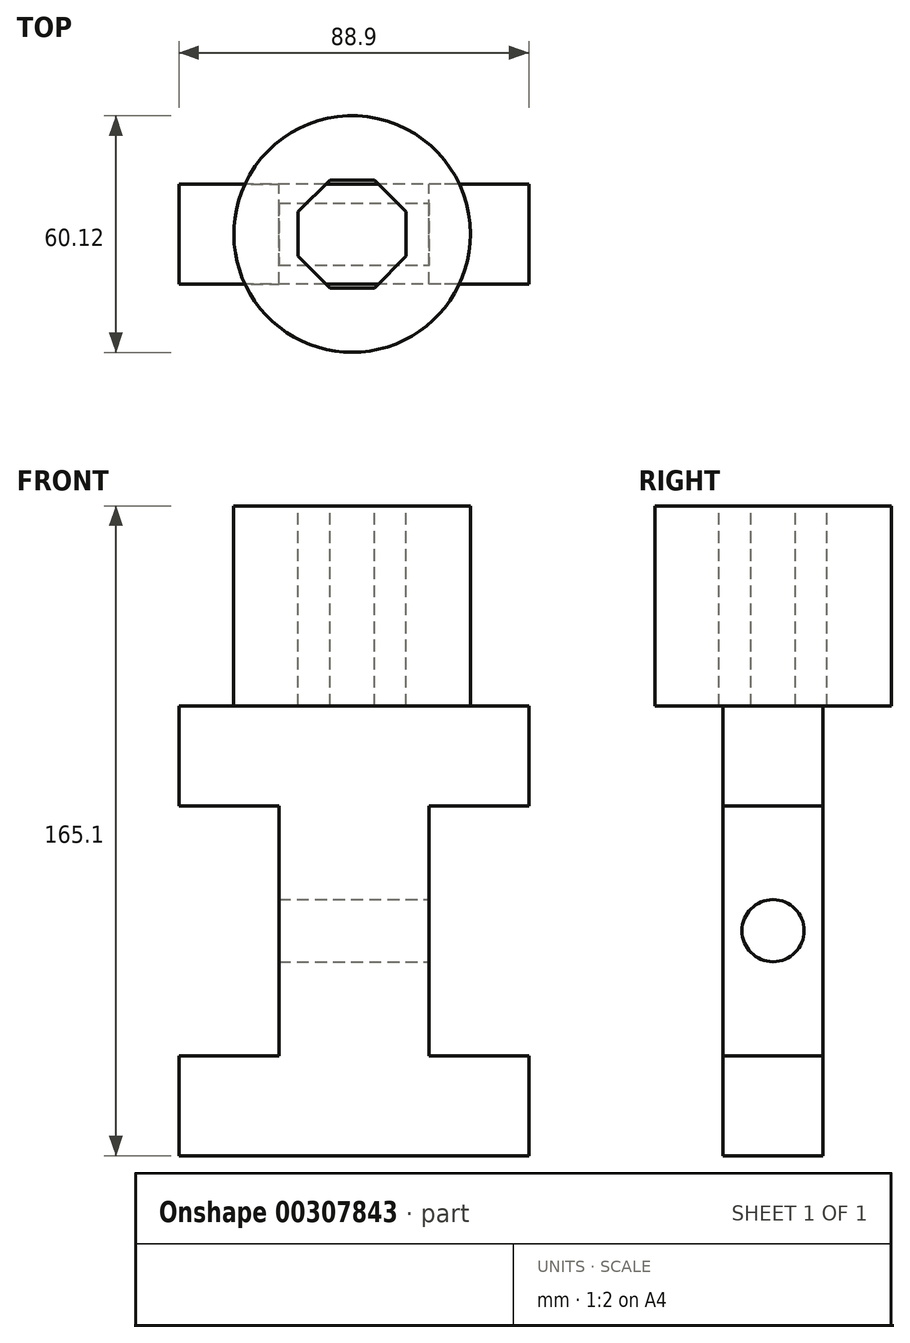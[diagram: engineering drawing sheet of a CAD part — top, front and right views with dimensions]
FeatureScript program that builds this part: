
annotation { "Feature Type Name" : "Feature", "Feature Type Description" : "" }
export const myFeature = defineFeature(function(context is Context, id is Id, definition is map)
    precondition{}
    {
        {
            var Q0;
            Q0=qCreatedBy(makeId("Front.planeOp"),FACE);
            var sketch = newSketch(context, id + "F0", { "sketchPlane" : qUnion([Q0])});
            skLineSegment(sketch, "E0", {"start": v(-44.02, -48.86) * mm, "end": v(44.88, -48.86) * mm});
            skLineSegment(sketch, "E1", {"start": v(44.88, -48.86) * mm, "end": v(44.88, -23.46) * mm});
            skLineSegment(sketch, "E2", {"start": v(44.88, -23.46) * mm, "end": v(19.48, -23.46) * mm});
            skLineSegment(sketch, "E3", {"start": v(19.48, -23.46) * mm, "end": v(19.48, 40.04) * mm});
            skLineSegment(sketch, "E4", {"start": v(19.48, 40.04) * mm, "end": v(44.88, 40.04) * mm});
            skLineSegment(sketch, "E5", {"start": v(44.88, 40.04) * mm, "end": v(44.88, 65.44) * mm});
            skLineSegment(sketch, "E6", {"start": v(44.88, 65.44) * mm, "end": v(-44.02, 65.44) * mm});
            skLineSegment(sketch, "E7", {"start": v(-44.02, 65.44) * mm, "end": v(-44.02, 40.04) * mm});
            skLineSegment(sketch, "E8", {"start": v(-44.02, 40.04) * mm, "end": v(-18.62, 40.04) * mm});
            skLineSegment(sketch, "E9", {"start": v(-18.62, 40.04) * mm, "end": v(-18.62, -23.46) * mm});
            skLineSegment(sketch, "E10", {"start": v(-18.62, -23.46) * mm, "end": v(-44.02, -23.46) * mm});
            skLineSegment(sketch, "E11", {"start": v(-44.02, -23.46) * mm, "end": v(-44.02, -48.86) * mm});
            skSolve(sketch);
        }
        {
            var Q0;
            Q0=makeQuery(id+"F0.imprint","IMPRINT",FACE,{"disambiguationData":[TD([[makeQuery(id+"F0.imprint","IMPRINT",EDGE,{"derivedFrom":sQuery(id+"F0.wireOp",EDGE,"E0")}),1.0]])]});
            extrude(context, id + "F1", {"entities" : qUnion([Q0]), "depth" : 25.4 * mm});
        }
        {
            var Q0;
            Q0=makeQuery(id+"F1.opExtrude","SWEPT_FACE",FACE,{"disambiguationData":[OSD([sQuery(id+"F0.wireOp",EDGE,"E3")])]});
            var sketch = newSketch(context, id + "F2", { "sketchPlane" : qUnion([Q0])});
            skCircle(sketch, "E12", {"center": v(-12.7, 8.3) * mm, "radius": 7.9 * mm});
            skPoint(sketch, "E12.centerSnap0", {"position": v(-12.7, 40.04) * mm});
            skPoint(sketch, "E12.centerSnap1", {"position": v(-25.4, 8.3) * mm});
            skSolve(sketch);
        }
        {
            var Q0;
            Q0=makeQuery(id+"F2.imprint","IMPRINT",FACE,{"disambiguationData":[TD([[makeQuery(id+"F2.imprint","IMPRINT",EDGE,{"derivedFrom":sQuery(id+"F2.wireOp",EDGE,"E12")}),1.0]])]});
            extrude(context, id + "F3", {"entities" : qUnion([Q0]), "operationType" : NewBodyOperationType.REMOVE, "endBound" : BoundingType.THROUGH_ALL, "oppositeDirection" : true, "depth" : 25.4 * mm});
        }
        {
            var Q0;
            Q0=makeQuery(id+"F1.opExtrude","SWEPT_FACE",FACE,{"disambiguationData":[OSD([sQuery(id+"F0.wireOp",EDGE,"E6")])]});
            var sketch = newSketch(context, id + "F4", { "sketchPlane" : qUnion([Q0])});
            skCircle(sketch, "E13", {"center": v(0, -12.7) * mm, "radius": 30.06 * mm});
            skPoint(sketch, "E13.centerSnap0", {"position": v(44.88, -12.7) * mm});
            skSolve(sketch);
        }
        {
            var Q0;
            {var subQ0=sQuery(id+"F4.wireOp",EDGE,"E13");var subQ1=makeQuery(id+"F1.opExtrude","CAP_EDGE",EDGE,{"disambiguationData":[OSD([sQuery(id+"F0.wireOp",EDGE,"E6")])],"isStart":true});var subQ2=makeQuery(id+"F4.imprint","INTERSECT",VERTEX,{"disambiguationData":[OD(0.0)],"derivedFrom":[subQ1,subQ0]});Q0=makeQuery(id+"F4.imprint","IMPRINT",FACE,{"disambiguationData":[TD([[makeQuery(id+"F4.imprint","IMPRINT",EDGE,{"disambiguationData":[TD([[subQ2,1.0]])],"derivedFrom":subQ0}),1.0]])]});}
            var Q1;
            {var subQ0=sQuery(id+"F4.wireOp",EDGE,"E13");var subQ1=makeQuery(id+"F1.opExtrude","CAP_EDGE",EDGE,{"disambiguationData":[OSD([sQuery(id+"F0.wireOp",EDGE,"E6")])],"isStart":false});var subQ2=makeQuery(id+"F4.imprint","INTERSECT",VERTEX,{"disambiguationData":[OD(0.0)],"derivedFrom":[subQ1,subQ0]});Q1=makeQuery(id+"F4.imprint","IMPRINT",FACE,{"disambiguationData":[TD([[makeQuery(id+"F4.imprint","IMPRINT",EDGE,{"disambiguationData":[TD([[subQ2,-1.0]])],"derivedFrom":subQ0}),1.0]])]});}
            var Q2;
            {var subQ0=sQuery(id+"F4.wireOp",EDGE,"E13");var subQ1=sQuery(id+"F0.wireOp",EDGE,"E6");var subQ2=makeQuery(id+"F1.opExtrude","CAP_EDGE",EDGE,{"disambiguationData":[OSD([subQ1])],"isStart":true});var subQ3=makeQuery(id+"F4.imprint","INTERSECT",VERTEX,{"disambiguationData":[OD(0.0)],"derivedFrom":[subQ2,subQ0]});Q2=makeQuery(id+"F4.imprint","IMPRINT",FACE,{"disambiguationData":[TD([[makeQuery(id+"F4.imprint","IMPRINT",EDGE,{"disambiguationData":[TD([[subQ3,-1.0]])],"derivedFrom":subQ0}),1.0]])]});}
            extrude(context, id + "F5", {"entities" : qUnion([Q0, Q1, Q2]), "operationType" : NewBodyOperationType.ADD, "depth" : 50.8 * mm});
        }
        {
            var Q0;
            Q0=makeQuery(id+"F5.opExtrude","CAP_FACE",FACE,{"disambiguationData":[OSD([sQuery(id+"F4.wireOp",EDGE,"E13")])],"isStart":false});
            var sketch = newSketch(context, id + "F6", { "sketchPlane" : qUnion([Q0])});
            skCircle(sketch, "E14.cCircle", {"center": v(0, -12.7) * mm, "radius": 13.68 * mm, "construction": true});
            skLineSegment(sketch, "E14.0", {"start": v(13.68, -7.03) * mm, "end": v(13.68, -18.37) * mm});
            skLineSegment(sketch, "E14.1", {"start": v(13.68, -18.37) * mm, "end": v(5.67, -26.38) * mm});
            skLineSegment(sketch, "E14.2", {"start": v(5.67, -26.38) * mm, "end": v(-5.67, -26.38) * mm});
            skLineSegment(sketch, "E14.3", {"start": v(-5.67, -26.38) * mm, "end": v(-13.68, -18.37) * mm});
            skLineSegment(sketch, "E14.4", {"start": v(-13.68, -18.37) * mm, "end": v(-13.68, -7.03) * mm});
            skLineSegment(sketch, "E14.5", {"start": v(-13.68, -7.03) * mm, "end": v(-5.67, 0.98) * mm});
            skLineSegment(sketch, "E14.6", {"start": v(-5.67, 0.98) * mm, "end": v(5.67, 0.98) * mm});
            skLineSegment(sketch, "E14.7", {"start": v(5.67, 0.98) * mm, "end": v(13.68, -7.03) * mm});
            skPoint(sketch, "E14.0.midPoint", {"position": v(13.68, -12.7) * mm});
            skSolve(sketch);
        }
        {
            var Q0;
            Q0=makeQuery(id+"F6.imprint","IMPRINT",FACE,{"disambiguationData":[TD([[makeQuery(id+"F6.imprint","IMPRINT",EDGE,{"derivedFrom":sQuery(id+"F6.wireOp",EDGE,"E14.0")}),-1.0]])]});
            extrude(context, id + "F7", {"entities" : qUnion([Q0]), "operationType" : NewBodyOperationType.REMOVE, "oppositeDirection" : true, "depth" : 50.8 * mm});
        }
    });
